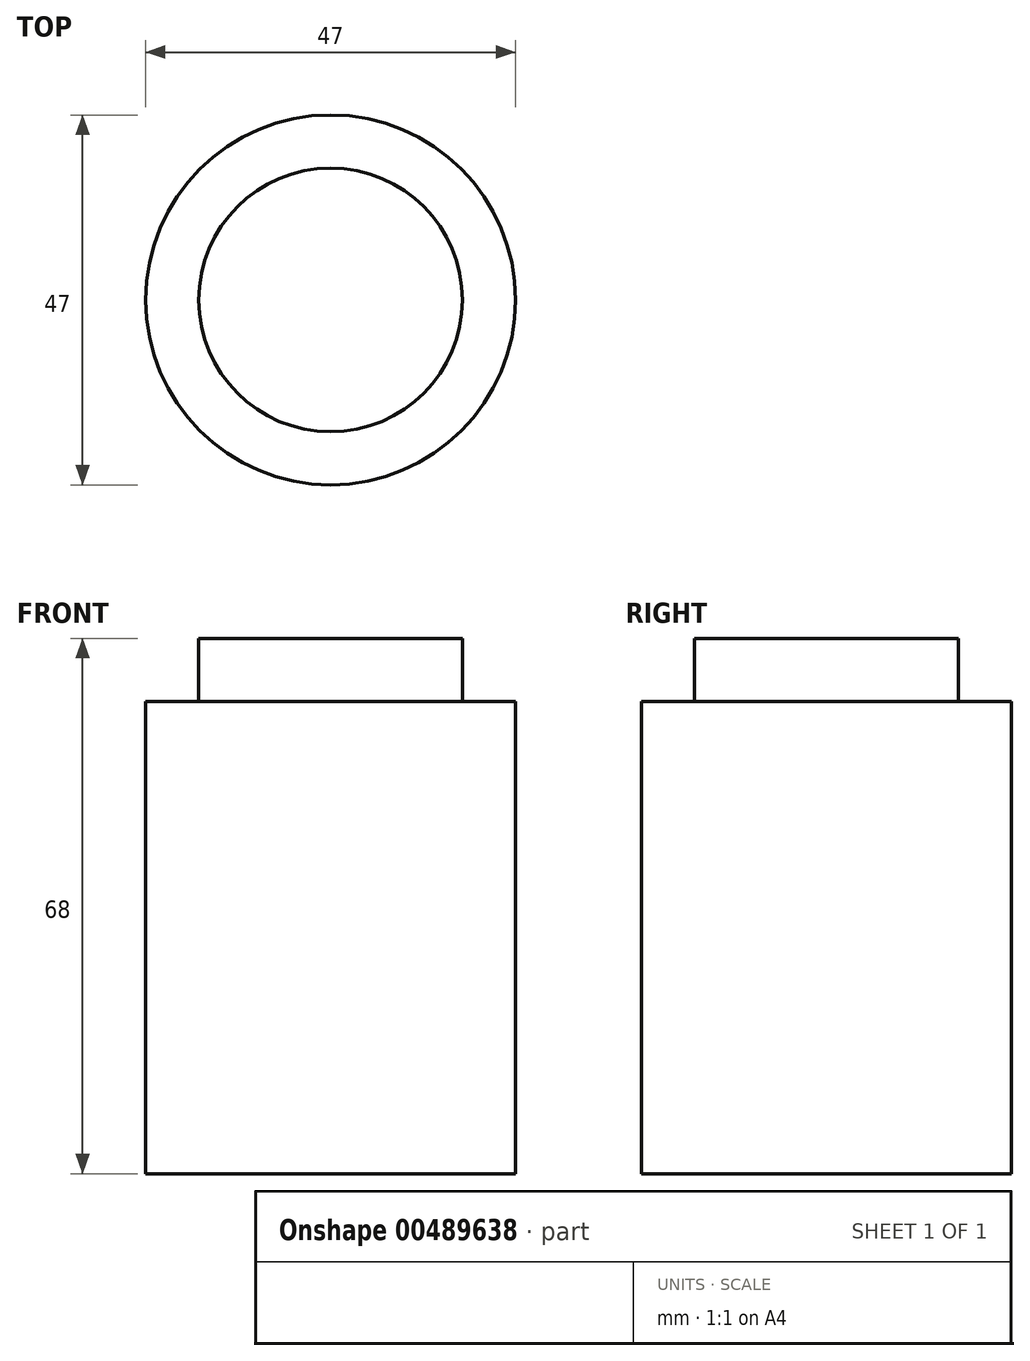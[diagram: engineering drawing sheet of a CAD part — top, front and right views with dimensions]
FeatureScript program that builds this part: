
annotation { "Feature Type Name" : "Feature", "Feature Type Description" : "" }
export const myFeature = defineFeature(function(context is Context, id is Id, definition is map)
    precondition{}
    {
        {
            var Q0;
            Q0=qCreatedBy(makeId("Top.planeOp"),FACE);
            var sketch = newSketch(context, id + "F0", { "sketchPlane" : qUnion([Q0])});
            skCircle(sketch, "E0", {"center": v(0, 0) * mm, "radius": 23.5 * mm});
            skSolve(sketch);
        }
        {
            var Q0;
            Q0 = qSketchRegion(id + "F0", true);
            extrude(context, id + "F1", {"entities" : qUnion([Q0]), "depth" : 60 * mm});
        }
        {
            var Q0;
            Q0=qCreatedBy(makeId("Top.planeOp"),FACE);
            var sketch = newSketch(context, id + "F2", { "sketchPlane" : qUnion([Q0])});
            skLineSegment(sketch, "E1.bottom", {"start": v(39.62, -56.76) * mm, "end": v(-39.62, -56.76) * mm});
            skLineSegment(sketch, "E1.top", {"start": v(39.62, 56.76) * mm, "end": v(-39.62, 56.76) * mm});
            skLineSegment(sketch, "E1.left", {"start": v(49.62, -46.76) * mm, "end": v(49.62, 46.76) * mm});
            skLineSegment(sketch, "E1.right", {"start": v(-49.62, -46.76) * mm, "end": v(-49.62, 46.76) * mm});
            skPoint(sketch, "E1.middle", {"position": v(0, 0) * mm});
            skPoint(sketch, "E2.visualSharp", {"position": v(-49.62, -56.76) * mm});
            skArc(sketch, "E2.filletArc", {"start": v(-49.62, -46.76) * mm, "mid": v(-46.69, -53.84) * mm, "end": v(-39.62, -56.76) * mm});
            skPoint(sketch, "E3.visualSharp", {"position": v(49.62, -56.76) * mm});
            skArc(sketch, "E3.filletArc", {"start": v(39.62, -56.76) * mm, "mid": v(46.69, -53.84) * mm, "end": v(49.62, -46.76) * mm});
            skPoint(sketch, "E4.visualSharp", {"position": v(49.62, 56.76) * mm});
            skArc(sketch, "E4.filletArc", {"start": v(49.62, 46.76) * mm, "mid": v(46.69, 53.84) * mm, "end": v(39.62, 56.76) * mm});
            skPoint(sketch, "E5.visualSharp", {"position": v(-49.62, 56.76) * mm});
            skArc(sketch, "E5.filletArc", {"start": v(-39.62, 56.76) * mm, "mid": v(-46.69, 53.84) * mm, "end": v(-49.62, 46.76) * mm});
            skSolve(sketch);
        }
        {
            var Q0;
            Q0=makeQuery(id+"F1.opExtrude","CAP_FACE",FACE,{"disambiguationData":[OSD([sQuery(id+"F0.wireOp",EDGE,"E0")])],"isStart":false});
            var sketch = newSketch(context, id + "F3", { "sketchPlane" : qUnion([Q0])});
            skCircle(sketch, "E6", {"center": v(0, 0) * mm, "radius": 35.98 * mm});
            skSolve(sketch);
        }
        {
            var Q0;
            Q0=makeQuery(id+"F3.imprint","IMPRINT",FACE,{"disambiguationData":[TD([[makeQuery(id+"F3.imprint","IMPRINT",EDGE,{"derivedFrom":makeQuery(id+"F1.opExtrude","CAP_EDGE",EDGE,{"disambiguationData":[OSD([sQuery(id+"F0.wireOp",EDGE,"E0")])],"isStart":false})}),1.0]])]});
            var sketch = newSketch(context, id + "F4", { "sketchPlane" : qUnion([Q0])});
            skCircle(sketch, "E7", {"center": v(0, 0) * mm, "radius": 16.75 * mm});
            skSolve(sketch);
        }
        {
            var Q0;
            Q0=makeQuery(id+"F4.imprint","IMPRINT",FACE,{"disambiguationData":[TD([[makeQuery(id+"F4.imprint","IMPRINT",EDGE,{"derivedFrom":sQuery(id+"F4.wireOp",EDGE,"E7")}),1.0]])]});
            extrude(context, id + "F5", {"entities" : qUnion([Q0]), "operationType" : NewBodyOperationType.ADD, "depth" : 8 * mm});
        }
        {
            var Q0;
            Q0 = qSketchRegion(id + "F2", true);
            var Q1;
            Q1 = qSketchRegion(id + "F3", true);
            var Q2;
            Q2=makeQuery(id+"F2.imprint","IMPRINT",FACE,{"disambiguationData":[TD([[makeQuery(id+"F2.imprint","IMPRINT",EDGE,{"derivedFrom":sQuery(id+"F2.wireOp",EDGE,"E1.bottom")}),-1.0]])]});
            var Q3;
            Q3=sQuery(id+"F3.wireOp",EDGE,"E6");
            loft(context, id + "F6", {"bodyType" : ToolBodyType.SURFACE, "sheetProfilesArray" : [{ "sheetProfileEntities" : qUnion([Q0]) }, { "sheetProfileEntities" : qUnion([Q1]) }], "wireProfilesArray" : [{ "wireProfileEntities" : qUnion([Q2]) }, { "wireProfileEntities" : qUnion([Q3]) }]});
        }
        {
            var Q0;
            Q0=makeQuery(id+"F5.opExtrude","CAP_FACE",FACE,{"disambiguationData":[OSD([sQuery(id+"F4.wireOp",EDGE,"E7")])],"isStart":false});
            var sketch = newSketch(context, id + "F7", { "sketchPlane" : qUnion([Q0])});
            skCircle(sketch, "E8", {"center": v(0, 0) * mm, "radius": 25.16 * mm});
            skSolve(sketch);
        }
        {
            var Q0;
            Q0 = qSketchRegion(id + "F7", true);
            var Q1;
            Q1 = qSketchRegion(id + "F3", true);
            var Q2;
            Q2 = qBodyType(qCreatedBy(id + "F3" ,EDGE), BodyType.WIRE);
            var Q3;
            Q3 = qBodyType(qCreatedBy(id + "F7" ,EDGE), BodyType.WIRE);
            loft(context, id + "F8", {"bodyType" : ToolBodyType.SURFACE, "startCondition" : LoftEndDerivativeType.TANGENT_TO_PROFILE, "startMagnitude" : 0, "endCondition" : LoftEndDerivativeType.TANGENT_TO_PROFILE, "endMagnitude" : 1.5, "sheetProfilesArray" : [{ "sheetProfileEntities" : qUnion([Q0]) }, { "sheetProfileEntities" : qUnion([Q1]) }], "wireProfilesArray" : [{ "wireProfileEntities" : qUnion([Q2]) }, { "wireProfileEntities" : qUnion([Q3]) }]});
        }
    });
